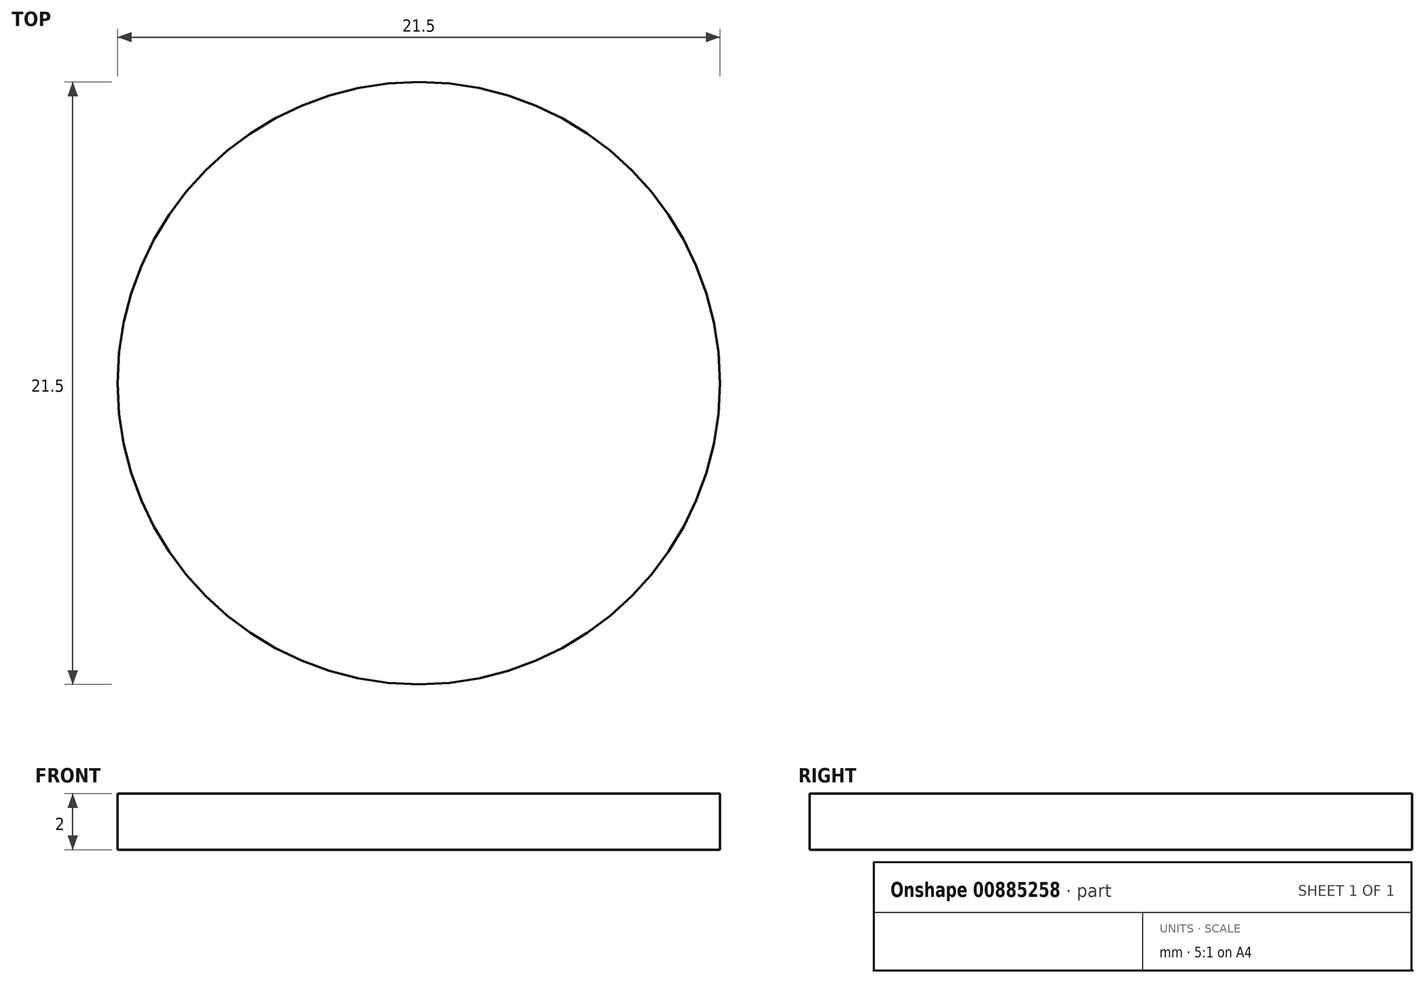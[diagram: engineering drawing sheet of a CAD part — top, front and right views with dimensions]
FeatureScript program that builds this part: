
annotation { "Feature Type Name" : "Feature", "Feature Type Description" : "" }
export const myFeature = defineFeature(function(context is Context, id is Id, definition is map)
    precondition{}
    {
        {
            var Q0;
            Q0=qCreatedBy(makeId("Top.planeOp"),FACE);
            var sketch = newSketch(context, id + "F0", { "sketchPlane" : qUnion([Q0])});
            skCircle(sketch, "E0", {"center": v(0, 0) * mm, "radius": 10.75 * mm});
            skSolve(sketch);
        }
        {
            var Q0;
            Q0=makeQuery(id+"F0.imprint","IMPRINT",FACE,{"disambiguationData":[TD([[makeQuery(id+"F0.imprint","IMPRINT",EDGE,{"derivedFrom":sQuery(id+"F0.wireOp",EDGE,"E0")}),1.0]])]});
            extrude(context, id + "F1", {"entities" : qUnion([Q0]), "depth" : 2 * mm, "offsetDistance" : 25 * mm});
        }
    });
